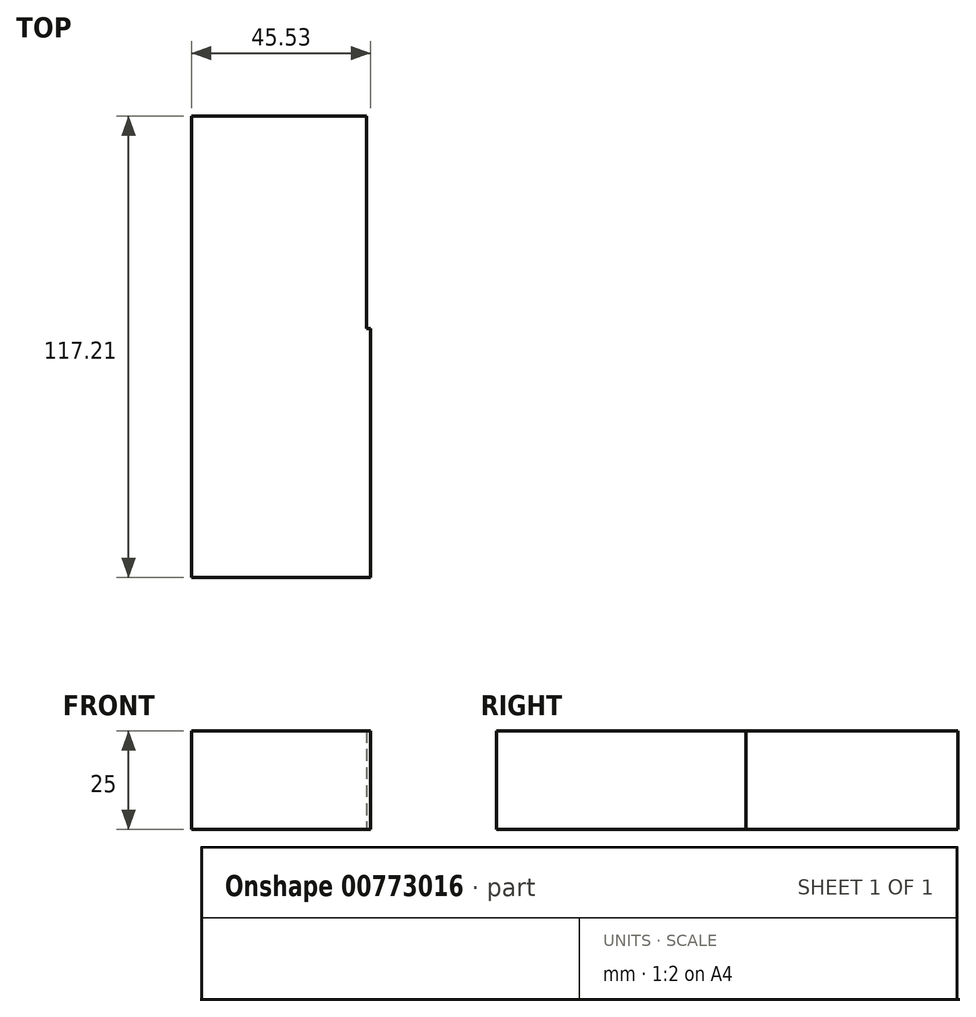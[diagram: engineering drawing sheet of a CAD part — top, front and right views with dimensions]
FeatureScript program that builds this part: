
annotation { "Feature Type Name" : "Feature", "Feature Type Description" : "" }
export const myFeature = defineFeature(function(context is Context, id is Id, definition is map)
    precondition{}
    {
        {
            var Q0;
            Q0=qCreatedBy(makeId("Top.planeOp"),FACE);
            var sketch = newSketch(context, id + "F0", { "sketchPlane" : qUnion([Q0])});
            skLineSegment(sketch, "E0", {"start": v(76.37, 21.44) * mm, "end": v(102.3, 21.44) * mm});
            skLineSegment(sketch, "E1.bottom", {"start": v(102.3, -2.86) * mm, "end": v(102.3, -2.86) * mm});
            skLineSegment(sketch, "E1.top", {"start": v(102.3, 21.44) * mm, "end": v(102.3, 21.44) * mm});
            skLineSegment(sketch, "E1.left", {"start": v(102.3, -2.86) * mm, "end": v(102.3, 21.44) * mm});
            skLineSegment(sketch, "E1.right", {"start": v(102.3, -2.86) * mm, "end": v(102.3, 21.44) * mm});
            skLineSegment(sketch, "E2.bottom", {"start": v(146.81, -32.47) * mm, "end": v(102.3, -32.47) * mm});
            skLineSegment(sketch, "E2.top", {"start": v(146.81, 21.44) * mm, "end": v(102.3, 21.44) * mm});
            skLineSegment(sketch, "E2.left", {"start": v(146.81, -32.47) * mm, "end": v(146.81, 21.44) * mm});
            skLineSegment(sketch, "E2.right", {"start": v(102.3, -32.47) * mm, "end": v(102.3, 21.44) * mm});
            skLineSegment(sketch, "E3.bottom", {"start": v(108.22, -32.47) * mm, "end": v(102.3, -32.47) * mm});
            skLineSegment(sketch, "E3.top", {"start": v(108.22, -32.47) * mm, "end": v(102.3, -32.47) * mm});
            skLineSegment(sketch, "E3.left", {"start": v(108.22, -32.47) * mm, "end": v(108.22, -32.47) * mm});
            skLineSegment(sketch, "E3.right", {"start": v(102.3, -32.47) * mm, "end": v(102.3, -32.47) * mm});
            skLineSegment(sketch, "E4.bottom", {"start": v(102.3, -32.47) * mm, "end": v(147.83, -32.47) * mm});
            skLineSegment(sketch, "E4.top", {"start": v(102.3, -95.77) * mm, "end": v(147.83, -95.77) * mm});
            skLineSegment(sketch, "E4.left", {"start": v(102.3, -32.47) * mm, "end": v(102.3, -95.77) * mm});
            skLineSegment(sketch, "E4.right", {"start": v(147.83, -32.47) * mm, "end": v(147.83, -95.77) * mm});
            skPoint(sketch, "E5.firstSnap0", {"position": v(125.07, -32.47) * mm});
            skPoint(sketch, "E5.oppositeSnap0", {"position": v(125.07, -32.47) * mm});
            skLineSegment(sketch, "E5.bottom", {"start": v(125.07, -59.62) * mm, "end": v(125.07, -59.62) * mm});
            skLineSegment(sketch, "E5.top", {"start": v(125.07, -69.83) * mm, "end": v(125.07, -69.83) * mm});
            skLineSegment(sketch, "E5.left", {"start": v(125.07, -59.62) * mm, "end": v(125.07, -69.83) * mm});
            skLineSegment(sketch, "E5.right", {"start": v(125.07, -59.62) * mm, "end": v(125.07, -69.83) * mm});
            skSolve(sketch);
        }
        {
            var Q0;
            Q0 = qSketchRegion(id + "F0", true);
            extrude(context, id + "F1", {"entities" : qUnion([Q0]), "depth" : 25 * mm, "offsetDistance" : 25 * mm});
        }
    });
